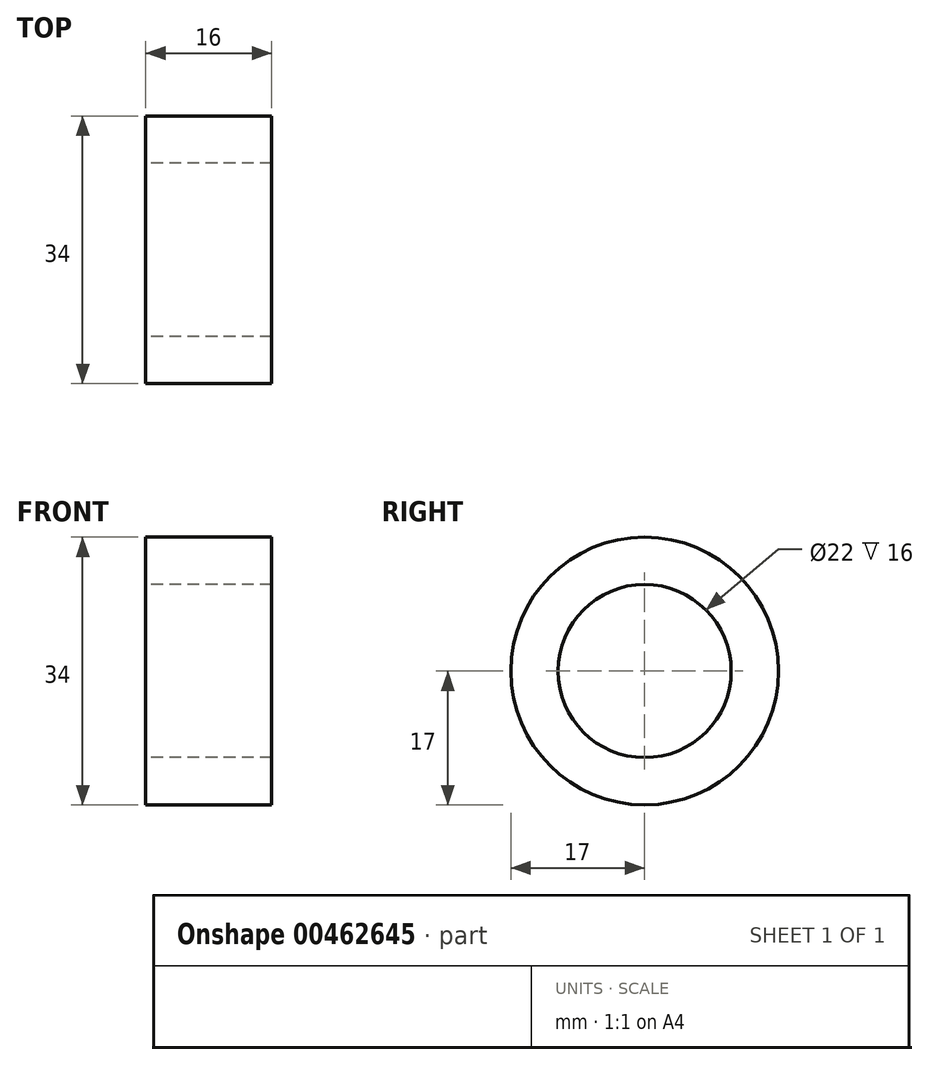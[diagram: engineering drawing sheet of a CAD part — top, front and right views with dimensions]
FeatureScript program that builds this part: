
annotation { "Feature Type Name" : "Feature", "Feature Type Description" : "" }
export const myFeature = defineFeature(function(context is Context, id is Id, definition is map)
    precondition{}
    {
        {
            var Q0;
            Q0=qCreatedBy(makeId("Front.planeOp"),FACE);
            var sketch = newSketch(context, id + "F0", { "sketchPlane" : qUnion([Q0])});
            skLineSegment(sketch, "E0", {"start": v(-81.32, 0) * mm, "end": v(83.79, 0) * mm, "construction": true});
            skLineSegment(sketch, "E1.bottom", {"start": v(8, 11) * mm, "end": v(-8, 11) * mm});
            skLineSegment(sketch, "E1.top", {"start": v(8, 17) * mm, "end": v(-8, 17) * mm});
            skLineSegment(sketch, "E1.left", {"start": v(8, 11) * mm, "end": v(8, 17) * mm});
            skLineSegment(sketch, "E1.right", {"start": v(-8, 11) * mm, "end": v(-8, 17) * mm});
            skPoint(sketch, "E1.middle", {"position": v(0, 14) * mm});
            skSolve(sketch);
        }
        {
            var Q0;
            Q0 = qSketchRegion(id + "F0", true);
            var Q1;
            Q1=sQuery(id+"F0.wireOp",EDGE,"E0");
            revolve(context, id + "F1", {"entities" : qUnion([Q0]), "axis" : qUnion([Q1]), "revolveType" : RevolveType.FULL});
        }
    });
